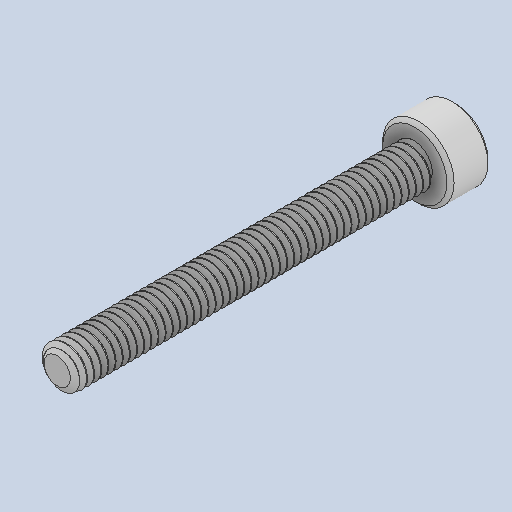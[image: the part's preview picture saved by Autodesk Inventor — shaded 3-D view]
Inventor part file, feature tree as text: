
AUTODESK INVENTOR PART (.ipt)
format: ipt  version: 2023 (Build 270158000, 158)  size: 1,315,328 bytes
history: native  units: in
note: dims shown in document units (in); Inventor stores cm internally (conversion verified against a paired STEP export)
features: chamfer x1
ambient origin geometry x8: Origin, YZ Plane, XZ Plane, XY Plane, X Axis, Y Axis, Z Axis, Center Point
bodies: Solid1 (feature_tree)
feature tree (1):
  chamfer  "Chamfer1"  [1 undecoded]
note: 1 required parameter value undecoded (feature->parameter linkage not recoverable at this tier; creation-order binding heuristic only, values carry confidence <= 0.55)
